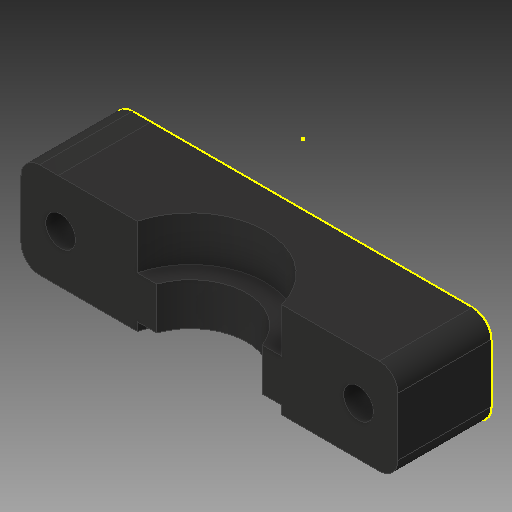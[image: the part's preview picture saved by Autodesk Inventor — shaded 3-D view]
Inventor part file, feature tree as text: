
AUTODESK INVENTOR PART (.ipt)
format: ipt  version: 2017 (Build 210142000, 142)  size: 143,872 bytes
history: native  units: mm
features: sketch x5, other x3
ambient origin geometry x8: Origin, YZ Plane, XZ Plane, XY Plane, X Axis, Y Axis, Z Axis, Center Point
bodies: Solid1 (feature_tree)
feature tree (8):
  other  "Hotend Clamp P1_MIR.ipt"
  other  "Solid1::Hotend Clamp P1_MIR.ipt"
  other  "TaggingFeature1"
  sketch  "Sketch1"  dims[d0=10.0mm]
  sketch  "Sketch2"
  sketch  "Sketch3"
  sketch  "Sketch4"
  sketch  "Sketch5"
